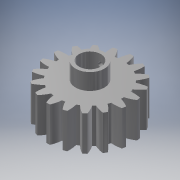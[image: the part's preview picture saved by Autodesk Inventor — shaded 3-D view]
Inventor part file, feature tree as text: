
AUTODESK INVENTOR PART (.ipt)
format: ipt  version: 2018 (Build 220112000, 112)  size: 254,464 bytes
history: native  units: mm (DEFAULTED — no unit token found)
features: other x7, sketch x5, extrude x4, plane x4, projected_geometry x1
ambient origin geometry x8: Origin, YZ Plane, XZ Plane, XY Plane, X Axis, Y Axis, Z Axis, Center Point
bodies: Body1 (feature_tree), Body2 (feature_tree)
feature tree (21):
  other  "Table"
  other  "Engranaje recto11-01"
  other  "Engranaje recto11-02"
  extrude  "Extrusion1"  Depth=25.0mm TaperAngle=0.0deg
  plane  "Work Plane2"
  plane  "Work Plane8"
  plane  "Work Plane9"
  other  "Engranaje recto"
  extrude  "Extrusión2"  Depth=10.0mm TaperAngle=0.0deg
  extrude  "Extrusión3"  Depth=1.745329mm TaperAngle=0.0deg
  plane  "Plano de trabajo11"
  extrude  "Extrusión4"  TaperAngle=0.0deg  [1 undecoded]
  sketch  "Sketch1"  dims[d0=60.0mm d1=25.0mm d2=0.0mm]
  sketch  "Sketch2"  dims[d3=54.0mm d4=10.0mm d5=0.0mm]
  other  "Srf1"
  sketch  "Boceto3"  dims[d16=108.0mm d17=0.0mm d34=1.745329mm]
  sketch  "Boceto4"  dims[d39=0.0mm d41=0.0mm]
  sketch  "Boceto5"  dims[d43=108.0mm d46=108.0mm d47=0.0mm d48=0.0mm d49=15.6mm d50=10.0mm d51=0.0mm d52=2.5mm d53=11.7mm d54=0.0mm d55=13.5mm d56=3.6mm d57=7.0mm d58=0.0mm d60=6.6mm]
  projected_geometry  "Contorno proyectado1"
  other  "Engranaje recto1"
  other  "Diámetro de separación"
note: 1 required parameter value undecoded (feature->parameter linkage not recoverable at this tier; creation-order binding heuristic only, values carry confidence <= 0.55)
